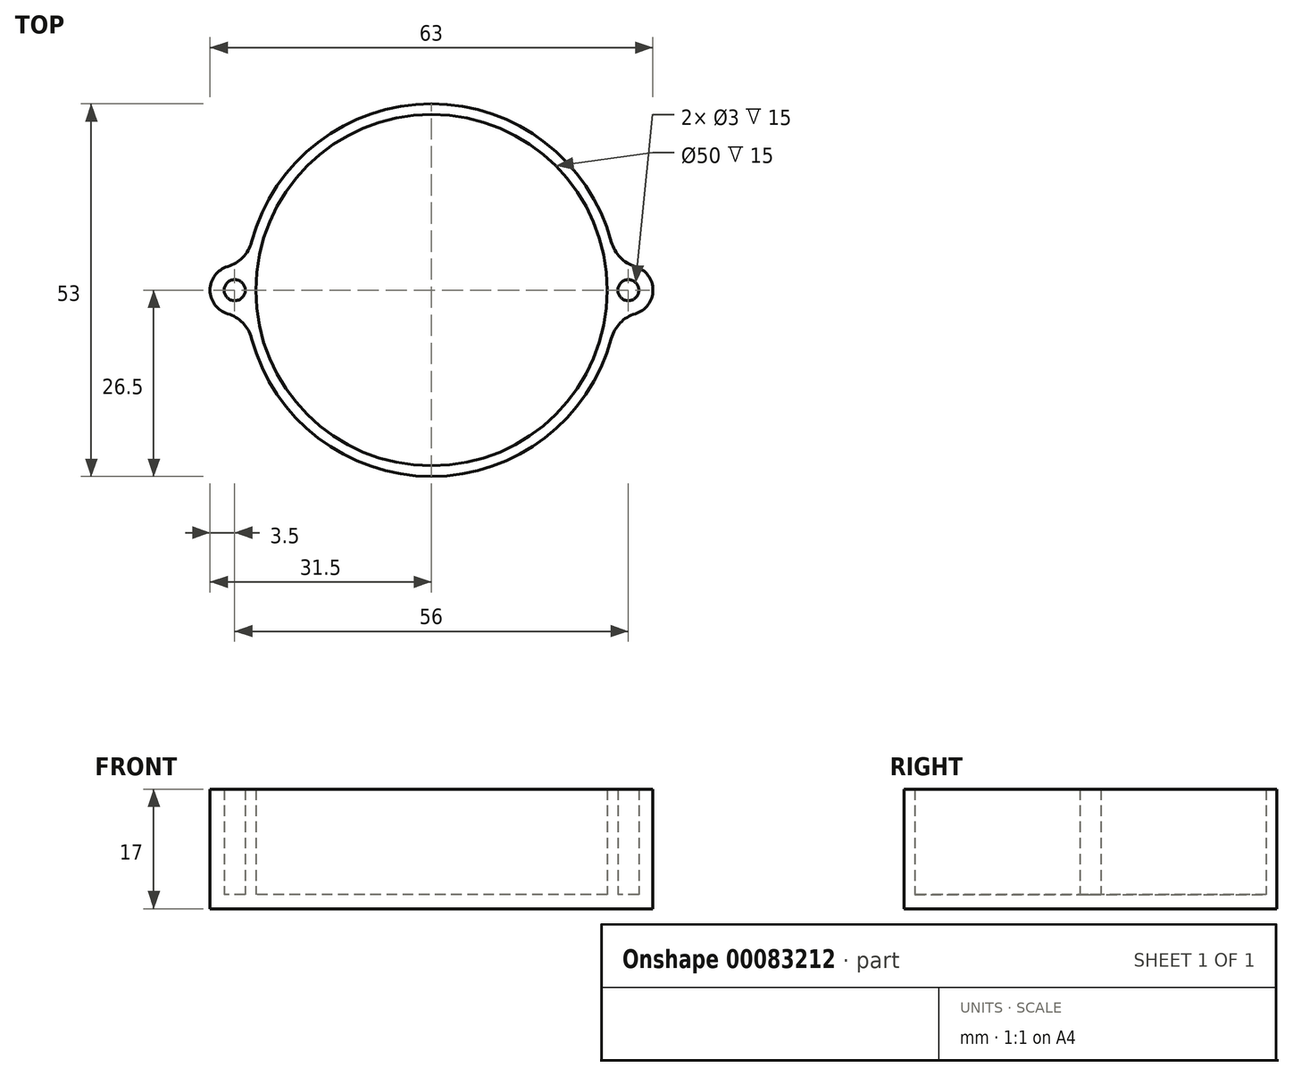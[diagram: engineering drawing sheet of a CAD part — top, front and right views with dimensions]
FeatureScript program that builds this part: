
annotation { "Feature Type Name" : "Feature", "Feature Type Description" : "" }
export const myFeature = defineFeature(function(context is Context, id is Id, definition is map)
    precondition{}
    {
        {
            var Q0;
            Q0=qCreatedBy(makeId("Top.planeOp"),FACE);
            var sketch = newSketch(context, id + "F0", { "sketchPlane" : qUnion([Q0])});
            skCircle(sketch, "E0", {"center": v(0, 0) * mm, "radius": 25 * mm});
            skCircle(sketch, "E1.0", {"center": v(0, 0) * mm, "radius": 26.5 * mm});
            skLineSegment(sketch, "E2", {"start": v(0, 0) * mm, "end": v(-30.1, 0) * mm, "construction": true});
            skLineSegment(sketch, "E3", {"start": v(-30.1, 0) * mm, "end": v(34.9, 0) * mm, "construction": true});
            skCircle(sketch, "E4", {"center": v(-28, 0) * mm, "radius": 1.5 * mm});
            skCircle(sketch, "E5", {"center": v(28, 0) * mm, "radius": 1.5 * mm});
            skCircle(sketch, "E6.0", {"center": v(28, 0) * mm, "radius": 3.5 * mm});
            skCircle(sketch, "E7.0", {"center": v(-28, 0) * mm, "radius": 3.5 * mm});
            skSolve(sketch);
        }
        {
            var Q0;
            Q0=qSketchRegion(id+"F0",true);
            extrude(context, id + "F1", {"entities" : qUnion([Q0]), "depth" : 17 * mm});
        }
        {
            var Q0;
            Q0=qSketchRegion(id+"F0",true);
            var Q1;
            Q1=makeQuery(id+"F0.imprint","IMPRINT",FACE,{"disambiguationData":[TD([[makeQuery(id+"F0.imprint","IMPRINT",EDGE,{"derivedFrom":sQuery(id+"F0.wireOp",EDGE,"E0")}),1.0]])]});
            var Q2;
            {var subQ0=sQuery(id+"F0.wireOp",EDGE,"E7.0");var subQ1=sQuery(id+"F0.wireOp",EDGE,"E0");var subQ2=makeQuery(id+"F0.imprint","INTERSECT",VERTEX,{"disambiguationData":[OD(0.0)],"derivedFrom":[subQ1,subQ0]});Q2=makeQuery(id+"F0.imprint","IMPRINT",FACE,{"disambiguationData":[TD([[makeQuery(id+"F0.imprint","IMPRINT",EDGE,{"disambiguationData":[TD([[subQ2,-1.0]])],"derivedFrom":subQ1}),1.0]])]});}
            var Q3;
            {var subQ0=sQuery(id+"F0.wireOp",EDGE,"E6.0");var subQ1=sQuery(id+"F0.wireOp",EDGE,"E0");var subQ2=makeQuery(id+"F0.imprint","INTERSECT",VERTEX,{"disambiguationData":[OD(0.0)],"derivedFrom":[subQ1,subQ0]});Q3=makeQuery(id+"F0.imprint","IMPRINT",FACE,{"disambiguationData":[TD([[makeQuery(id+"F0.imprint","IMPRINT",EDGE,{"disambiguationData":[TD([[subQ2,1.0]])],"derivedFrom":subQ1}),1.0]])]});}
            var Q4;
            Q4=makeQuery(id+"F0.imprint","IMPRINT",FACE,{"disambiguationData":[TD([[makeQuery(id+"F0.imprint","IMPRINT",EDGE,{"derivedFrom":sQuery(id+"F0.wireOp",EDGE,"E4")}),1.0]])]});
            var Q5;
            Q5=makeQuery(id+"F0.imprint","IMPRINT",FACE,{"disambiguationData":[TD([[makeQuery(id+"F0.imprint","IMPRINT",EDGE,{"derivedFrom":sQuery(id+"F0.wireOp",EDGE,"E5")}),1.0]])]});
            extrude(context, id + "F2", {"entities" : qUnion([Q0, Q1, Q2, Q3, Q4, Q5]), "operationType" : NewBodyOperationType.ADD, "depth" : 2 * mm});
        }
        {
            var Q0;
            {var subQ0=sQuery(id+"F0.wireOp",EDGE,"E7.0");var subQ1=sQuery(id+"F0.wireOp",EDGE,"E1.0");Q0=makeQuery(id+"F1.opExtrude","SWEPT_EDGE",EDGE,{"disambiguationData":[OSD([subQ1,subQ0]),TDD([makeQuery(id+"F0.imprint","INTERSECT",VERTEX,{"disambiguationData":[OD(0.0)],"derivedFrom":[subQ1,subQ0]})])]});}
            var Q1;
            {var subQ0=sQuery(id+"F0.wireOp",EDGE,"E7.0");var subQ1=sQuery(id+"F0.wireOp",EDGE,"E1.0");Q1=makeQuery(id+"F1.opExtrude","SWEPT_EDGE",EDGE,{"disambiguationData":[OSD([subQ1,subQ0]),TDD([makeQuery(id+"F0.imprint","INTERSECT",VERTEX,{"disambiguationData":[OD(1.0)],"derivedFrom":[subQ1,subQ0]})])]});}
            var Q2;
            {var subQ0=sQuery(id+"F0.wireOp",EDGE,"E6.0");var subQ1=sQuery(id+"F0.wireOp",EDGE,"E1.0");Q2=makeQuery(id+"F1.opExtrude","SWEPT_EDGE",EDGE,{"disambiguationData":[OSD([subQ1,subQ0]),TDD([makeQuery(id+"F0.imprint","INTERSECT",VERTEX,{"disambiguationData":[OD(1.0)],"derivedFrom":[subQ1,subQ0]})])]});}
            var Q3;
            {var subQ0=sQuery(id+"F0.wireOp",EDGE,"E6.0");var subQ1=sQuery(id+"F0.wireOp",EDGE,"E1.0");Q3=makeQuery(id+"F1.opExtrude","SWEPT_EDGE",EDGE,{"disambiguationData":[OSD([subQ1,subQ0]),TDD([makeQuery(id+"F0.imprint","INTERSECT",VERTEX,{"disambiguationData":[OD(0.0)],"derivedFrom":[subQ1,subQ0]})])]});}
            fillet(context, id + "F3", {"entities" : qUnion([Q0, Q1, Q2, Q3]), "radius" : 5 * mm, "tangentPropagation" : true, "allowEdgeOverflow" : false});
        }
    });
